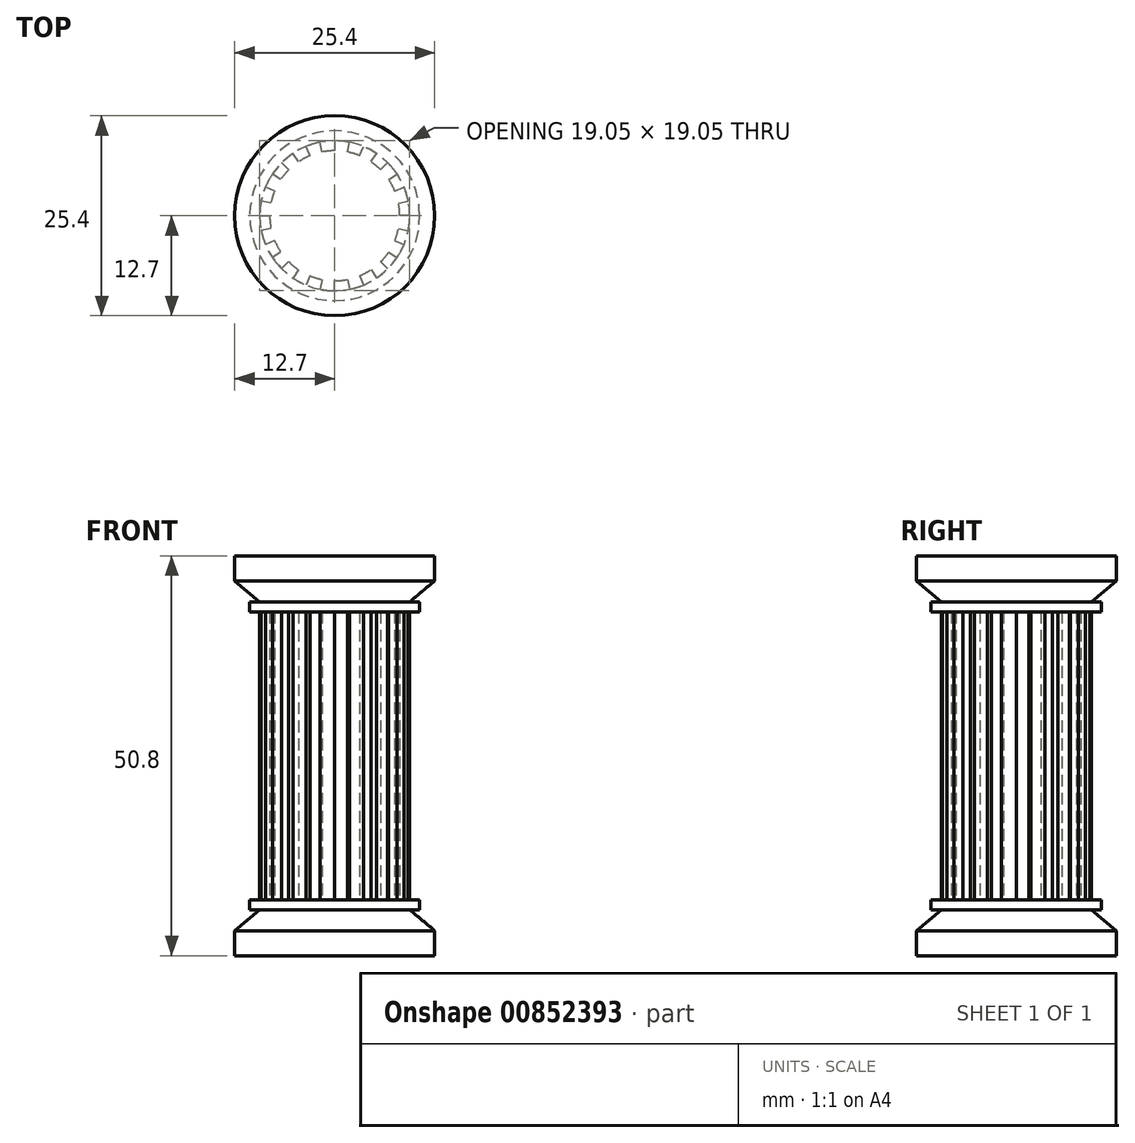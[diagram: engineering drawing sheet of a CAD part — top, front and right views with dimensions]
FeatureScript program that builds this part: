
annotation { "Feature Type Name" : "Feature", "Feature Type Description" : "" }
export const myFeature = defineFeature(function(context is Context, id is Id, definition is map)
    precondition{}
    {
        {
            var Q0;
            Q0=qCreatedBy(makeId("Right.planeOp"),FACE);
            var sketch = newSketch(context, id + "F0", { "sketchPlane" : qUnion([Q0])});
            skLineSegment(sketch, "E0", {"start": v(0, 0) * mm, "end": v(-12.7, 0) * mm});
            skLineSegment(sketch, "E1", {"start": v(-9.52, 44.96) * mm, "end": v(-12.7, 47.63) * mm});
            skLineSegment(sketch, "E2", {"start": v(-12.7, 47.63) * mm, "end": v(-12.7, 50.8) * mm});
            skLineSegment(sketch, "E3", {"start": v(-12.7, 50.8) * mm, "end": v(0, 50.8) * mm});
            skLineSegment(sketch, "E4", {"start": v(0, 50.8) * mm, "end": v(0, 0) * mm});
            skLineSegment(sketch, "E5", {"start": v(-12.7, 0) * mm, "end": v(-12.7, 3.18) * mm});
            skLineSegment(sketch, "E6", {"start": v(-12.7, 3.18) * mm, "end": v(-9.53, 5.84) * mm});
            skLineSegment(sketch, "E7.bottom", {"start": v(-9.53, 5.84) * mm, "end": v(-10.8, 5.84) * mm});
            skLineSegment(sketch, "E7.top", {"start": v(-9.53, 7.1) * mm, "end": v(-10.8, 7.1) * mm});
            skLineSegment(sketch, "E7.right", {"start": v(-10.8, 5.84) * mm, "end": v(-10.8, 7.1) * mm});
            skLineSegment(sketch, "E8.bottom", {"start": v(-9.52, 44.96) * mm, "end": v(-10.8, 44.96) * mm});
            skLineSegment(sketch, "E8.top", {"start": v(-9.52, 43.7) * mm, "end": v(-10.8, 43.7) * mm});
            skLineSegment(sketch, "E8.right", {"start": v(-10.8, 44.96) * mm, "end": v(-10.8, 43.7) * mm});
            skLineSegment(sketch, "E9", {"start": v(-9.52, 43.7) * mm, "end": v(-9.53, 7.1) * mm});
            skSolve(sketch);
        }
        {
            var Q0;
            Q0 = qSketchRegion(id + "F0", true);
            var Q1;
            Q1=sQuery(id+"F0.wireOp",EDGE,"E4");
            revolve(context, id + "F1", {"surfaceOperationType" : NewSurfaceOperationType.NEW, "entities" : qUnion([Q0]), "axis" : qUnion([Q1]), "revolveType" : RevolveType.FULL});
        }
        {
            var Q0;
            Q0=makeQuery(id+"F1.opRevolve","SWEPT_FACE",FACE,{"disambiguationData":[OSD([sQuery(id+"F0.wireOp",EDGE,"E7.top")])]});
            var sketch = newSketch(context, id + "F2", { "sketchPlane" : qUnion([Q0])});
            skArc(sketch, "E10.0", {"start": v(3.65, -8.8) * mm, "mid": v(4.5, -8.4) * mm, "end": v(5.3, -7.92) * mm});
            skLineSegment(sketch, "E11", {"start": v(0, -9.52) * mm, "end": v(0, -8.25) * mm});
            skLineSegment(sketch, "E12", {"start": v(5.84, -5.84) * mm, "end": v(6.74, -6.74) * mm});
            skLineSegment(sketch, "E13", {"start": v(3.16, -7.63) * mm, "end": v(3.65, -8.8) * mm});
            skLineSegment(sketch, "E14", {"start": v(7.63, -3.16) * mm, "end": v(8.8, -3.65) * mm});
            skLineSegment(sketch, "E15", {"start": v(4.59, -6.86) * mm, "end": v(5.3, -7.92) * mm});
            skLineSegment(sketch, "E16", {"start": v(1.61, -8.1) * mm, "end": v(1.86, -9.34) * mm});
            skLineSegment(sketch, "E17", {"start": v(6.86, -4.59) * mm, "end": v(7.92, -5.3) * mm});
            skLineSegment(sketch, "E18", {"start": v(8.1, -1.61) * mm, "end": v(9.34, -1.86) * mm});
            skArc(sketch, "E19", {"start": v(3.16, -7.63) * mm, "mid": v(3.9, -7.28) * mm, "end": v(4.59, -6.86) * mm});
            skArc(sketch, "E20.trimOffspring", {"start": v(5.84, -5.84) * mm, "mid": v(6.38, -5.24) * mm, "end": v(6.86, -4.59) * mm});
            skArc(sketch, "E21.trimOffspring", {"start": v(7.63, -3.16) * mm, "mid": v(7.9, -2.4) * mm, "end": v(8.1, -1.61) * mm});
            skArc(sketch, "E22.trimOffspring", {"start": v(0, -8.25) * mm, "mid": v(0.8, -8.22) * mm, "end": v(1.61, -8.1) * mm});
            skArc(sketch, "E23.trimOffspring", {"start": v(6.74, -6.74) * mm, "mid": v(7.36, -6.04) * mm, "end": v(7.92, -5.3) * mm});
            skArc(sketch, "E24.trimOffspring", {"start": v(8.8, -3.65) * mm, "mid": v(9.11, -2.76) * mm, "end": v(9.34, -1.86) * mm});
            skArc(sketch, "E25.trimOffspring", {"start": v(0, -9.52) * mm, "mid": v(0.93, -9.48) * mm, "end": v(1.86, -9.34) * mm});
            skPoint(sketch, "E26.start.orphan", {"position": v(9.52, 0) * mm});
            skArc(sketch, "E27.1.0", {"start": v(-8.8, -3.65) * mm, "mid": v(-8.4, -4.5) * mm, "end": v(-7.92, -5.3) * mm});
            skArc(sketch, "E27.1.2", {"start": v(-7.63, -3.16) * mm, "mid": v(-7.28, -3.9) * mm, "end": v(-6.86, -4.59) * mm});
            skArc(sketch, "E27.1.3", {"start": v(-9.52, 0) * mm, "mid": v(-9.48, -0.93) * mm, "end": v(-9.34, -1.86) * mm});
            skArc(sketch, "E27.1.4", {"start": v(-8.25, 0) * mm, "mid": v(-8.22, -0.8) * mm, "end": v(-8.1, -1.61) * mm});
            skLineSegment(sketch, "E27.1.5", {"start": v(-6.86, -4.59) * mm, "end": v(-7.92, -5.3) * mm});
            skLineSegment(sketch, "E27.1.6", {"start": v(-8.1, -1.61) * mm, "end": v(-9.34, -1.86) * mm});
            skLineSegment(sketch, "E27.1.7", {"start": v(-7.63, -3.16) * mm, "end": v(-8.8, -3.65) * mm});
            skLineSegment(sketch, "E27.1.8", {"start": v(-9.52, 0) * mm, "end": v(-8.25, 0) * mm});
            skLineSegment(sketch, "E27.1.9", {"start": v(-4.59, -6.86) * mm, "end": v(-5.3, -7.92) * mm});
            skArc(sketch, "E27.1.10", {"start": v(-3.65, -8.8) * mm, "mid": v(-2.76, -9.11) * mm, "end": v(-1.86, -9.34) * mm});
            skLineSegment(sketch, "E27.1.11", {"start": v(-5.84, -5.84) * mm, "end": v(-6.74, -6.74) * mm});
            skLineSegment(sketch, "E27.1.12", {"start": v(-3.16, -7.63) * mm, "end": v(-3.65, -8.8) * mm});
            skArc(sketch, "E27.1.13", {"start": v(-5.84, -5.84) * mm, "mid": v(-5.24, -6.38) * mm, "end": v(-4.59, -6.86) * mm});
            skLineSegment(sketch, "E27.1.14", {"start": v(-1.61, -8.1) * mm, "end": v(-1.86, -9.34) * mm});
            skPoint(sketch, "E27.1.15", {"position": v(0, -9.52) * mm});
            skArc(sketch, "E27.1.16", {"start": v(-6.74, -6.74) * mm, "mid": v(-6.04, -7.36) * mm, "end": v(-5.3, -7.92) * mm});
            skArc(sketch, "E27.1.17", {"start": v(-3.16, -7.63) * mm, "mid": v(-2.4, -7.9) * mm, "end": v(-1.61, -8.1) * mm});
            skArc(sketch, "E27.2.0", {"start": v(-3.65, 8.8) * mm, "mid": v(-4.5, 8.4) * mm, "end": v(-5.3, 7.92) * mm});
            skArc(sketch, "E27.2.2", {"start": v(-3.16, 7.63) * mm, "mid": v(-3.9, 7.28) * mm, "end": v(-4.59, 6.86) * mm});
            skArc(sketch, "E27.2.3", {"start": v(0, 9.52) * mm, "mid": v(-0.93, 9.48) * mm, "end": v(-1.86, 9.34) * mm});
            skArc(sketch, "E27.2.4", {"start": v(0, 8.25) * mm, "mid": v(-0.8, 8.22) * mm, "end": v(-1.61, 8.1) * mm});
            skLineSegment(sketch, "E27.2.5", {"start": v(-4.59, 6.86) * mm, "end": v(-5.3, 7.92) * mm});
            skLineSegment(sketch, "E27.2.6", {"start": v(-1.61, 8.1) * mm, "end": v(-1.86, 9.34) * mm});
            skLineSegment(sketch, "E27.2.7", {"start": v(-3.16, 7.63) * mm, "end": v(-3.65, 8.8) * mm});
            skLineSegment(sketch, "E27.2.8", {"start": v(0, 9.52) * mm, "end": v(0, 8.25) * mm});
            skLineSegment(sketch, "E27.2.9", {"start": v(-6.86, 4.59) * mm, "end": v(-7.92, 5.3) * mm});
            skArc(sketch, "E27.2.10", {"start": v(-8.8, 3.65) * mm, "mid": v(-9.11, 2.76) * mm, "end": v(-9.34, 1.86) * mm});
            skLineSegment(sketch, "E27.2.11", {"start": v(-5.84, 5.84) * mm, "end": v(-6.74, 6.74) * mm});
            skLineSegment(sketch, "E27.2.12", {"start": v(-7.63, 3.16) * mm, "end": v(-8.8, 3.65) * mm});
            skArc(sketch, "E27.2.13", {"start": v(-5.84, 5.84) * mm, "mid": v(-6.38, 5.24) * mm, "end": v(-6.86, 4.59) * mm});
            skLineSegment(sketch, "E27.2.14", {"start": v(-8.1, 1.61) * mm, "end": v(-9.34, 1.86) * mm});
            skPoint(sketch, "E27.2.15", {"position": v(-9.52, 0) * mm});
            skArc(sketch, "E27.2.16", {"start": v(-6.74, 6.74) * mm, "mid": v(-7.36, 6.04) * mm, "end": v(-7.92, 5.3) * mm});
            skArc(sketch, "E27.2.17", {"start": v(-7.63, 3.16) * mm, "mid": v(-7.9, 2.4) * mm, "end": v(-8.1, 1.61) * mm});
            skArc(sketch, "E27.3.0", {"start": v(8.8, 3.65) * mm, "mid": v(8.4, 4.5) * mm, "end": v(7.92, 5.3) * mm});
            skArc(sketch, "E27.3.2", {"start": v(7.63, 3.16) * mm, "mid": v(7.28, 3.9) * mm, "end": v(6.86, 4.59) * mm});
            skArc(sketch, "E27.3.3", {"start": v(9.52, 0) * mm, "mid": v(9.48, 0.93) * mm, "end": v(9.34, 1.86) * mm});
            skArc(sketch, "E27.3.4", {"start": v(8.25, 0) * mm, "mid": v(8.22, 0.8) * mm, "end": v(8.1, 1.61) * mm});
            skLineSegment(sketch, "E27.3.5", {"start": v(6.86, 4.59) * mm, "end": v(7.92, 5.3) * mm});
            skLineSegment(sketch, "E27.3.6", {"start": v(8.1, 1.61) * mm, "end": v(9.34, 1.86) * mm});
            skLineSegment(sketch, "E27.3.7", {"start": v(7.63, 3.16) * mm, "end": v(8.8, 3.65) * mm});
            skLineSegment(sketch, "E27.3.8", {"start": v(9.52, 0) * mm, "end": v(8.25, 0) * mm});
            skLineSegment(sketch, "E27.3.9", {"start": v(4.59, 6.86) * mm, "end": v(5.3, 7.92) * mm});
            skArc(sketch, "E27.3.10", {"start": v(3.65, 8.8) * mm, "mid": v(2.76, 9.11) * mm, "end": v(1.86, 9.34) * mm});
            skLineSegment(sketch, "E27.3.11", {"start": v(5.84, 5.84) * mm, "end": v(6.74, 6.74) * mm});
            skLineSegment(sketch, "E27.3.12", {"start": v(3.16, 7.63) * mm, "end": v(3.65, 8.8) * mm});
            skArc(sketch, "E27.3.13", {"start": v(5.84, 5.84) * mm, "mid": v(5.24, 6.38) * mm, "end": v(4.59, 6.86) * mm});
            skLineSegment(sketch, "E27.3.14", {"start": v(1.61, 8.1) * mm, "end": v(1.86, 9.34) * mm});
            skPoint(sketch, "E27.3.15", {"position": v(0, 9.52) * mm});
            skArc(sketch, "E27.3.16", {"start": v(6.74, 6.74) * mm, "mid": v(6.04, 7.36) * mm, "end": v(5.3, 7.92) * mm});
            skArc(sketch, "E27.3.17", {"start": v(3.16, 7.63) * mm, "mid": v(2.4, 7.9) * mm, "end": v(1.61, 8.1) * mm});
            skLineSegment(sketch, "E27.anchor1", {"start": v(0, 0) * mm, "end": v(0, -9.52) * mm, "construction": true});
            skLineSegment(sketch, "E27.anchor2", {"start": v(0, 0) * mm, "end": v(9.52, 0) * mm, "construction": true});
            skSolve(sketch);
        }
        {
            var Q0;
            Q0 = qSketchRegion(id + "F2", true);
            var Q1;
            Q1=makeQuery(id+"F1.opRevolve","SWEPT_FACE",FACE,{"disambiguationData":[OSD([sQuery(id+"F0.wireOp",EDGE,"E8.top")])]});
            extrude(context, id + "F3", {"entities" : qUnion([Q0]), "operationType" : NewBodyOperationType.REMOVE, "endBound" : BoundingType.UP_TO_SURFACE, "depth" : 33.65 * mm, "endBoundEntityFace" : qUnion([Q1]), "offsetDistance" : 25.4 * mm});
        }
    });
